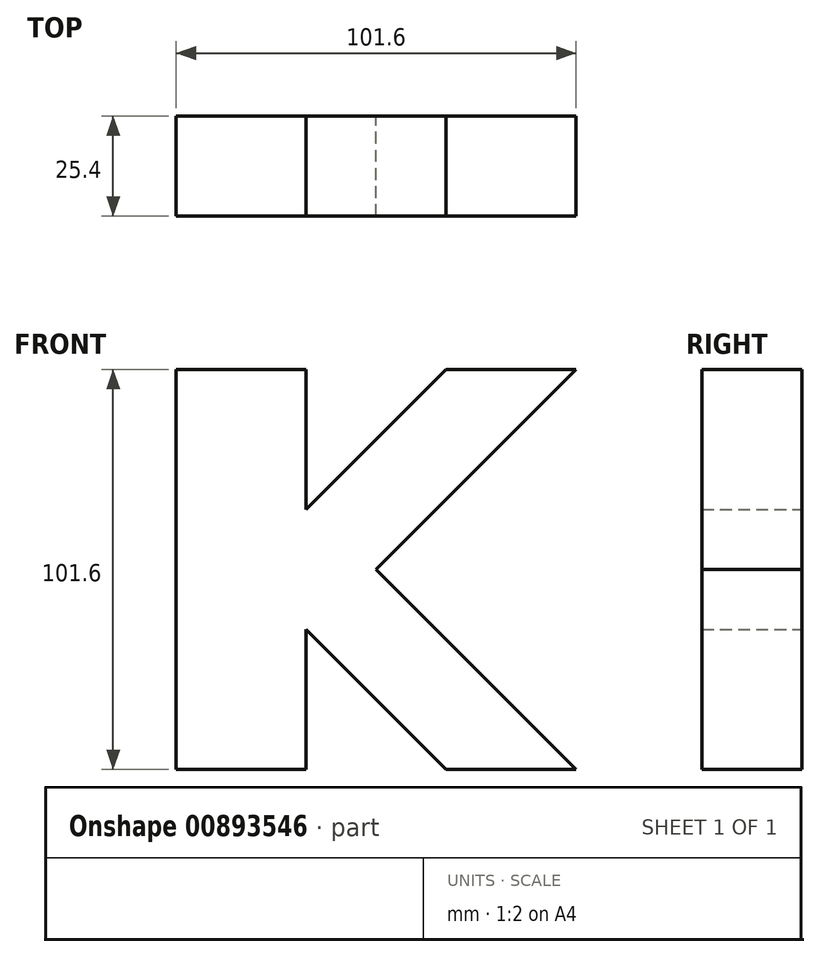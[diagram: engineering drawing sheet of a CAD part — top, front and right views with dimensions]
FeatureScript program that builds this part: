
annotation { "Feature Type Name" : "Feature", "Feature Type Description" : "" }
export const myFeature = defineFeature(function(context is Context, id is Id, definition is map)
    precondition{}
    {
        {
            var Q0;
            Q0=qCreatedBy(makeId("Front.planeOp"),FACE);
            var sketch = newSketch(context, id + "F0", { "sketchPlane" : qUnion([Q0])});
            skLineSegment(sketch, "E0", {"start": v(0, 0) * mm, "end": v(0, 101.6) * mm});
            skLineSegment(sketch, "E1", {"start": v(0, 101.6) * mm, "end": v(33.02, 101.6) * mm});
            skLineSegment(sketch, "E2", {"start": v(33.02, 101.6) * mm, "end": v(33.02, 66.04) * mm});
            skLineSegment(sketch, "E3", {"start": v(33.02, 66.04) * mm, "end": v(68.58, 101.6) * mm});
            skLineSegment(sketch, "E4", {"start": v(68.58, 101.6) * mm, "end": v(101.6, 101.6) * mm});
            skLineSegment(sketch, "E5", {"start": v(101.6, 101.6) * mm, "end": v(50.8, 50.8) * mm});
            skLineSegment(sketch, "E6", {"start": v(50.8, 50.8) * mm, "end": v(101.6, 0) * mm});
            skLineSegment(sketch, "E7", {"start": v(101.6, 0) * mm, "end": v(68.58, 0) * mm});
            skLineSegment(sketch, "E8", {"start": v(68.58, 0) * mm, "end": v(33.02, 35.56) * mm});
            skLineSegment(sketch, "E9", {"start": v(33.02, 35.56) * mm, "end": v(33.02, 0) * mm});
            skLineSegment(sketch, "E10", {"start": v(33.02, 0) * mm, "end": v(0, 0) * mm});
            skPoint(sketch, "E11", {"position": v(0, 50.8) * mm});
            skSolve(sketch);
        }
        {
            var Q0;
            Q0 = qSketchRegion(id + "F0", true);
            extrude(context, id + "F1", {"entities" : qUnion([Q0]), "depth" : 25.4 * mm, "offsetDistance" : 25.4 * mm});
        }
    });
